# Revit family: 12. Секция сотового увлажнения ANR U2
name_source: partatom
category: Оборудование
revit_build: Autodesk Revit 2016 (Build: 20161004_0715(x64)
units: mm (PartAtom-declared; Revit-internal decimal feet)

## family parameters
Всегда вертикально = Да
На основе рабочей плоскости = Нет
Общий = Нет
При загрузке вырезать с полостями = Нет
Размер круглого соединителя = Использовать диаметр
Тип детали = Нормальный
Точка расчета площади = Нет

## types (16) — shared parameters
D залива и перелива = 25 мм
d слива = 19 мм
h = 130 мм
Д = 1100 мм
Д1 = 1080 мм
Д2 = 270 мм
Единица измерения = шт.
Завод изготовитель = KORF
Ключевая пометка = Вентиляция
Материал = Сталь серая
Наименование и тех.хар-ка = Секция сотового увлажнения
Напряжение U,В = 1-220
Раздел = ОВ
Синий = Синий
высота ножек = 120 мм

## per-type parameters (varying)
| type | А | А1 | Б | Б1 | Высота | Мощность насоса, Вт | Середина | Сила тока J, А | Тип, марка, обозначение | Ширина | Эффективность увлажнения, % |
| ANR 6 U2.1 | 1100 мм | 1080 мм | 1100 мм | 1080 мм | 1025 мм | 190 Вт | 670 мм | 6.7 | ANR 6 U2.1 | 1025 мм | 85 |
| ANR 6 U2.2 | 1100 мм | 1080 мм | 1100 мм | 1080 мм | 1025 мм | 190 Вт | 670 мм | 6.7 | ANR 6 U2.2 | 1025 мм | 95 |
| ANR 7 U2.1 | 1100 мм | 1080 мм | 1320 мм | 1300 мм | 1245 мм | 190 Вт | 780 мм | 6.7 | ANR 7 U2.1 | 1025 мм | 85 |
| ANR  7 U2.2 | 1100 мм | 1080 мм | 1320 мм | 1300 мм | 1245 мм | 190 Вт | 780 мм | 6.7 | ANR 7 U2.2 | 1025 мм | 95 |
| ANR 8 U2.1 | 1320 мм | 1300 мм | 1320 мм | 1300 мм | 1245 мм | 190 Вт | 780 мм | 6.7 | ANR 8 U2.1 | 1245 мм | 85 |
| ANR 8 U2.2 | 1320 мм | 1300 мм | 1320 мм | 1300 мм | 1245 мм | 190 Вт | 780 мм | 6.7 | ANR 8 U2.2 | 1245 мм | 95 |
| ANR 12 U2.1 | 1435 мм | 1415 мм | 1435 мм | 1415 мм | 1360 мм | 190 Вт | 838 мм | 6.7 | ANR 12 U2.1 | 1360 мм | 85 |
| ANR 12 U2.2 | 1435 мм | 1415 мм | 1435 мм | 1415 мм | 1360 мм | 190 Вт | 838 мм | 6.7 | ANR 12 U2.2 | 1360 мм | 95 |
| ANR 20 U2.1 | 1660 мм | 1640 мм | 1660 мм | 1640 мм | 1585 мм | 350 Вт | 950 мм | 14 | ANR 20 U2.1 | 1585 мм | 85 |
| ANR 20 U2.2 | 1660 мм | 1640 мм | 1660 мм | 1640 мм | 1585 мм | 350 Вт | 950 мм | 14 | ANR 20 U2.2 | 1585 мм | 95 |
| ANR 25 U2.1 | 2045 мм | 2025 мм | 2045 мм | 2025 мм | 1970 мм | 350 Вт | 1143 мм | 14 | ANR 25 U2.1 | 1970 мм | 85 |
| ANR 25 U2.2 | 2045 мм | 2025 мм | 2045 мм | 2025 мм | 1970 мм | 350 Вт | 1143 мм | 14 | ANR 25 U2.2 | 1970 мм | 95 |
| ANR 30 U2.1 | 2485 мм | 2465 мм | 2045 мм | 2025 мм | 1970 мм | 350 Вт | 1143 мм | 14 | ANR 30 U2.1 | 2410 мм | 85 |
| ANR 30 U2.2 | 2485 мм | 2465 мм | 2045 мм | 2025 мм | 1970 мм | 350 Вт | 1143 мм | 14 | ANR 30 U2.2 | 2410 мм | 95 |
| ANR 35 U2.1 | 2485 мм | 2465 мм | 2485 мм | 2465 мм | 2410 мм | 350 Вт | 1363 мм | 14 | ANR 35 U2.1 | 2410 мм | 85 |
| ANR 35 U2.2 | 2485 мм | 2465 мм | 2485 мм | 2465 мм | 2410 мм | 350 Вт | 1363 мм | 14 | ANR 35 U2.2 | 2410 мм | 95 |
